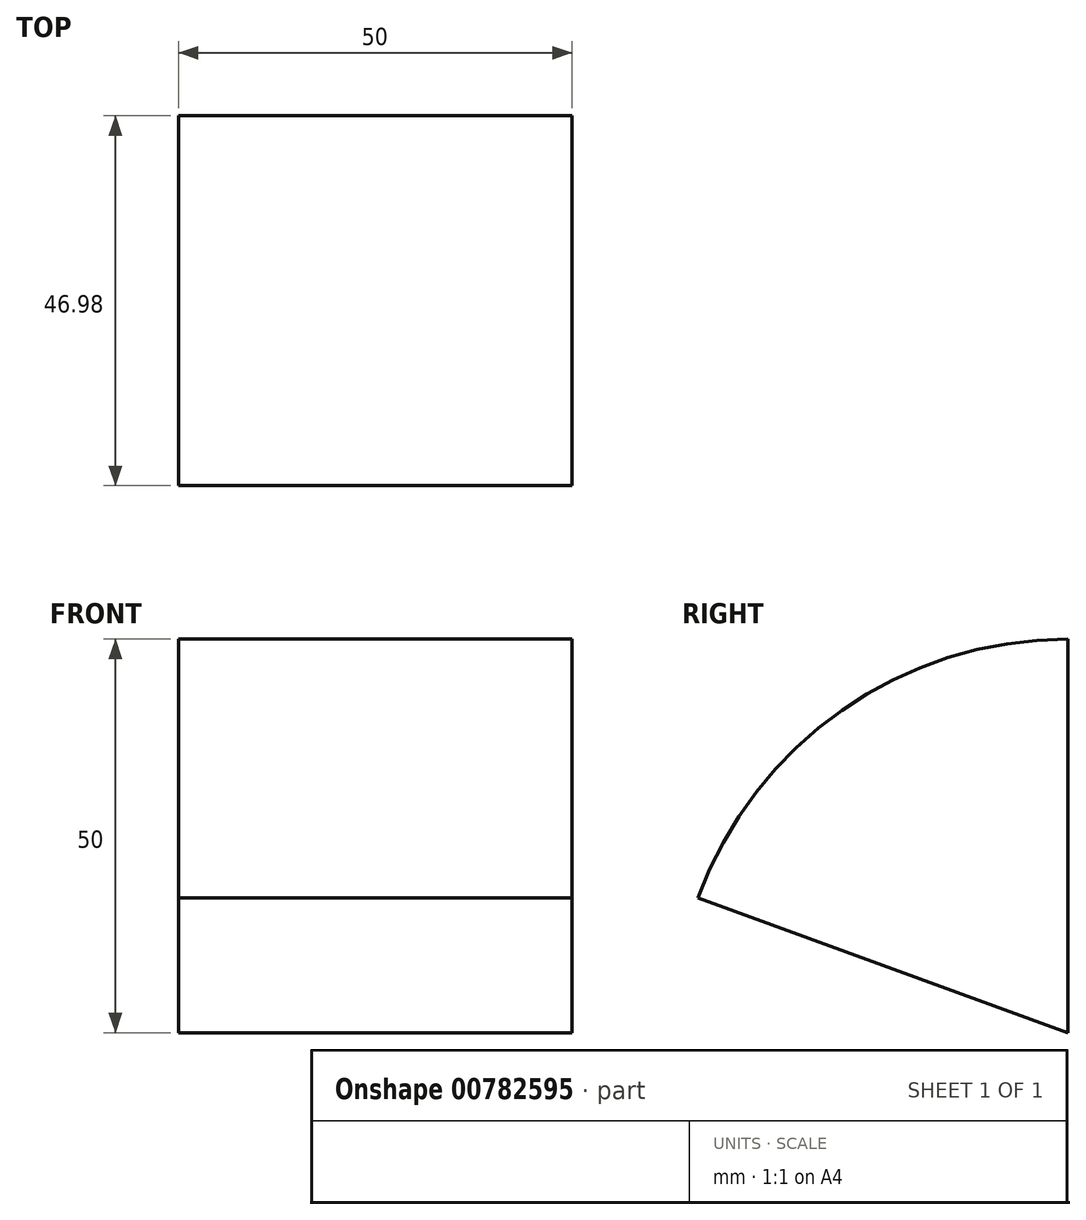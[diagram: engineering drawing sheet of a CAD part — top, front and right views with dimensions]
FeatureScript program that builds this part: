
annotation { "Feature Type Name" : "Feature", "Feature Type Description" : "" }
export const myFeature = defineFeature(function(context is Context, id is Id, definition is map)
    precondition{}
    {
        {
            var Q0;
            Q0=qCreatedBy(makeId("Front.planeOp"),FACE);
            var sketch = newSketch(context, id + "F0", { "sketchPlane" : qUnion([Q0])});
            skLineSegment(sketch, "E0.bottom", {"start": v(0, 0) * mm, "end": v(50, 0) * mm});
            skLineSegment(sketch, "E0.top", {"start": v(0, 50) * mm, "end": v(50, 50) * mm});
            skLineSegment(sketch, "E0.left", {"start": v(0, 0) * mm, "end": v(0, 50) * mm});
            skLineSegment(sketch, "E0.right", {"start": v(50, 0) * mm, "end": v(50, 50) * mm});
            skSolve(sketch);
        }
        {
            var Q0;
            Q0=makeQuery(id+"F0.imprint","IMPRINT",FACE,{"disambiguationData":[TD([[makeQuery(id+"F0.imprint","IMPRINT",EDGE,{"derivedFrom":sQuery(id+"F0.wireOp",EDGE,"E0.bottom")}),1.0]])]});
            var Q1;
            Q1=sQuery(id+"F0.wireOp",EDGE,"E0.bottom");
            revolve(context, id + "F1", {"surfaceOperationType" : NewSurfaceOperationType.NEW, "entities" : qUnion([Q0]), "axis" : qUnion([Q1]), "revolveType" : RevolveType.ONE_DIRECTION, "angle" : 70 * degree});
        }
    });
